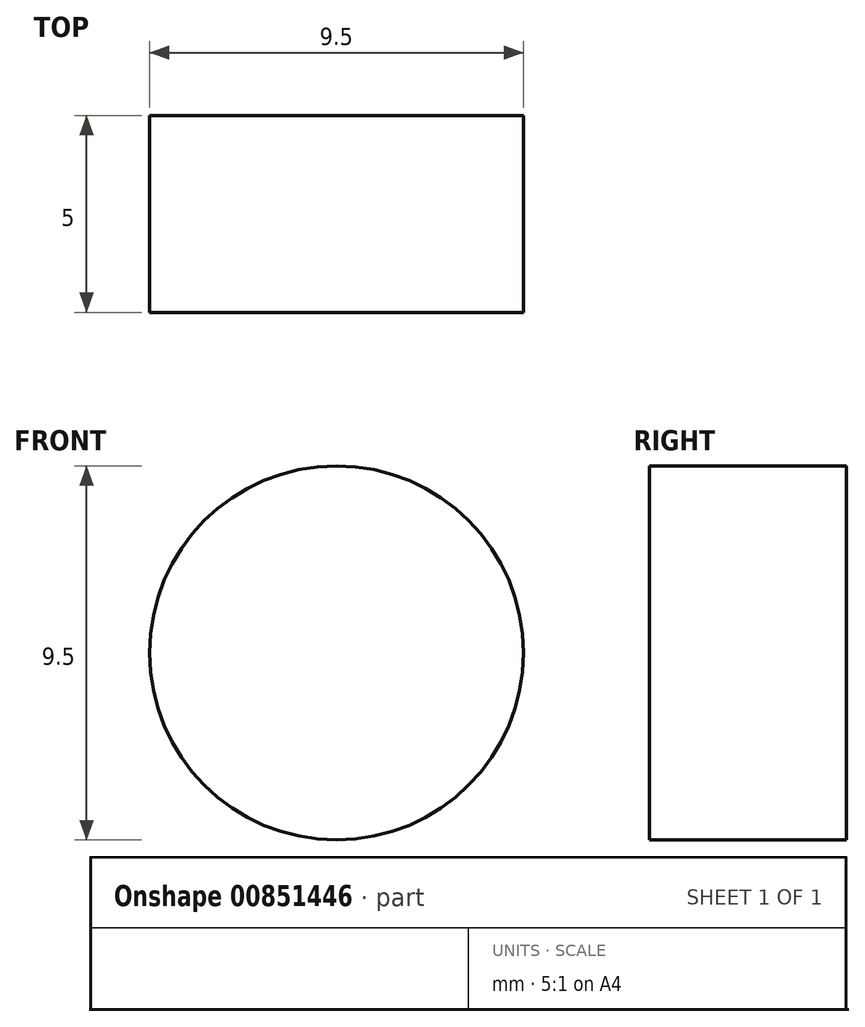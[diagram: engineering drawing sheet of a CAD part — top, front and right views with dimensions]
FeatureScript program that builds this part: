
annotation { "Feature Type Name" : "Feature", "Feature Type Description" : "" }
export const myFeature = defineFeature(function(context is Context, id is Id, definition is map)
    precondition{}
    {
        {
            var Q0;
            Q0=qCreatedBy(makeId("Front.planeOp"),FACE);
            var sketch = newSketch(context, id + "F0", { "sketchPlane" : qUnion([Q0])});
            skCircle(sketch, "E0", {"center": v(0, 0) * mm, "radius": 4.75 * mm});
            skSolve(sketch);
        }
        {
            var Q0;
            Q0 = qSketchRegion(id + "F0", true);
            extrude(context, id + "F1", {"entities" : qUnion([Q0]), "depth" : 5 * mm, "offsetDistance" : 25.4 * mm});
        }
    });
